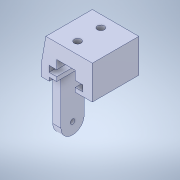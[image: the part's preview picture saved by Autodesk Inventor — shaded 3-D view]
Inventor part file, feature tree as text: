
AUTODESK INVENTOR PART (.ipt)
format: ipt  version: 2020 (Build 240168000, 168)  size: 141,824 bytes
history: mixed  units: mm
features: other x2, extrude x1, sketch x1, imported_body x1
ambient origin geometry x8: Origin, YZ Plane, XZ Plane, XY Plane, X Axis, Y Axis, Z Axis, Center Point
bodies: Body1 (imported_parasolid)
feature tree (5):
  other  "Твердое тело1"
  extrude  "Выдавливание1"  Depth=0.5mm
  sketch  "Эскиз1"
  other  "Cut-Extrude3"
  imported_body  NMx_Import_Brep_tag  [imported B-rep: ~31 faces, bbox_mm=[22.0, 37.0, 20.0]]
